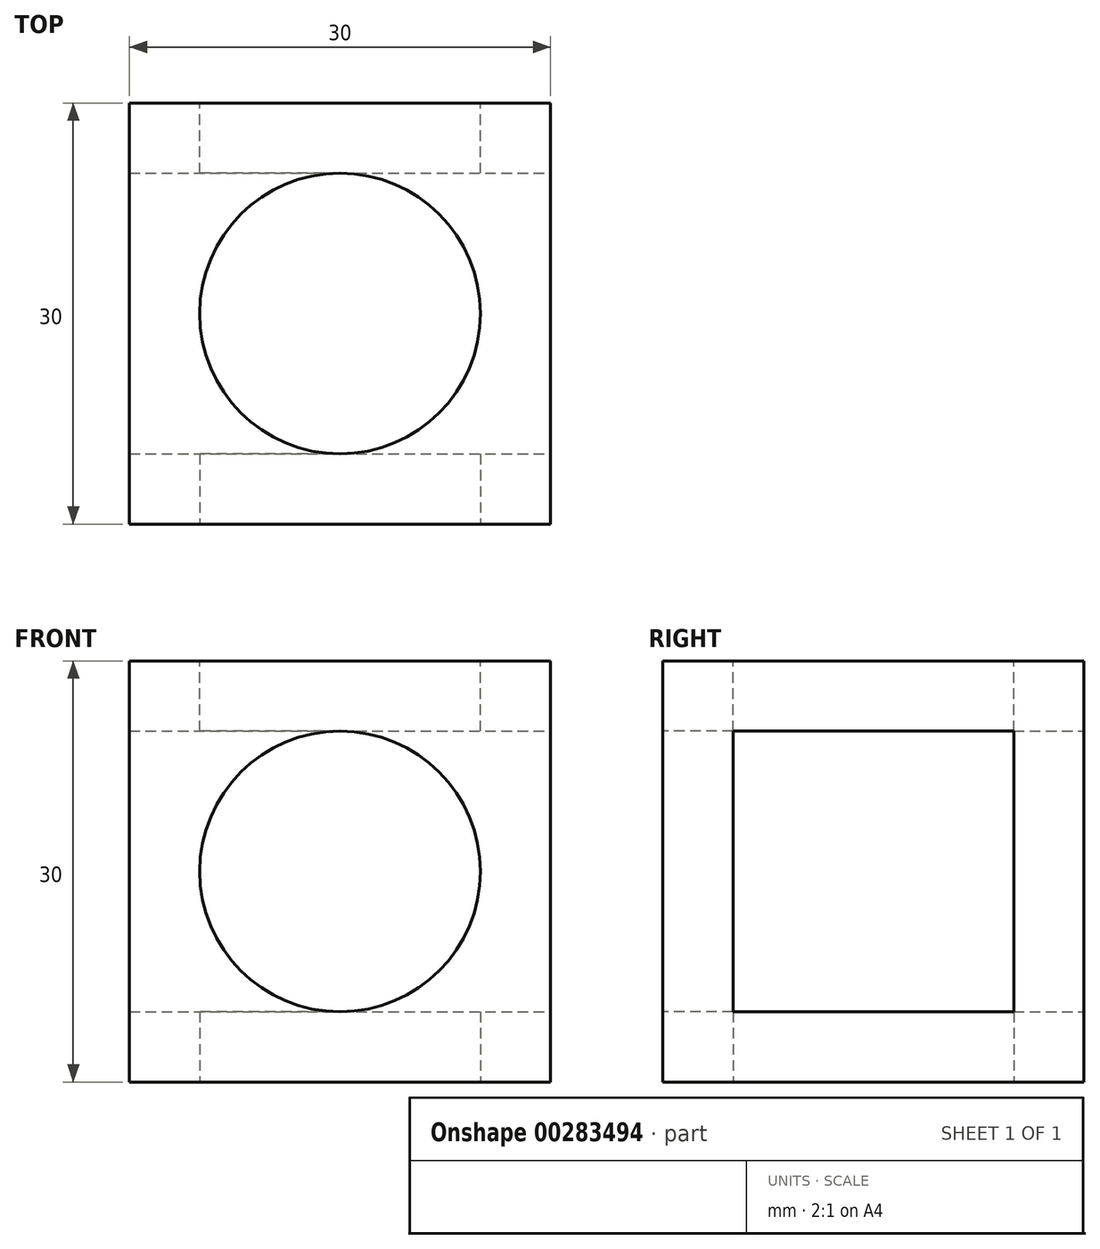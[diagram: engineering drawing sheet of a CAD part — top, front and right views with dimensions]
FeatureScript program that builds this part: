
annotation { "Feature Type Name" : "Feature", "Feature Type Description" : "" }
export const myFeature = defineFeature(function(context is Context, id is Id, definition is map)
    precondition{}
    {
        {
            var Q0;
            Q0=qCreatedBy(makeId("Right.planeOp"),FACE);
            var sketch = newSketch(context, id + "F0", { "sketchPlane" : qUnion([Q0])});
            skLineSegment(sketch, "E0.bottom", {"start": v(15, 15) * mm, "end": v(-15, 15) * mm});
            skLineSegment(sketch, "E0.top", {"start": v(15, -15) * mm, "end": v(-15, -15) * mm});
            skLineSegment(sketch, "E0.left", {"start": v(15, 15) * mm, "end": v(15, -15) * mm});
            skLineSegment(sketch, "E0.right", {"start": v(-15, 15) * mm, "end": v(-15, -15) * mm});
            skPoint(sketch, "E0.middle", {"position": v(0, 0) * mm});
            skSolve(sketch);
        }
        {
            var Q0;
            Q0=makeQuery(id+"F0.imprint","IMPRINT",FACE,{"disambiguationData":[TD([[makeQuery(id+"F0.imprint","IMPRINT",EDGE,{"derivedFrom":sQuery(id+"F0.wireOp",EDGE,"E0.bottom")}),1.0]])]});
            extrude(context, id + "F1", {"entities" : qUnion([Q0]), "depth" : 30 * mm});
        }
        {
            var Q0;
            Q0=makeQuery(id+"F1.opExtrude","CAP_FACE",FACE,{"disambiguationData":[OSD([sQuery(id+"F0.wireOp",EDGE,"E0.bottom"),sQuery(id+"F0.wireOp",EDGE,"E0.top"),sQuery(id+"F0.wireOp",EDGE,"E0.left"),sQuery(id+"F0.wireOp",EDGE,"E0.right")])],"isStart":false});
            var sketch = newSketch(context, id + "F2", { "sketchPlane" : qUnion([Q0])});
            skLineSegment(sketch, "E1.bottom", {"start": v(10, 10) * mm, "end": v(-10, 10) * mm});
            skLineSegment(sketch, "E1.top", {"start": v(10, -10) * mm, "end": v(-10, -10) * mm});
            skLineSegment(sketch, "E1.left", {"start": v(10, 10) * mm, "end": v(10, -10) * mm});
            skLineSegment(sketch, "E1.right", {"start": v(-10, 10) * mm, "end": v(-10, -10) * mm});
            skPoint(sketch, "E1.middle", {"position": v(0, 0) * mm});
            skSolve(sketch);
        }
        {
            var Q0;
            Q0=makeQuery(id+"F2.imprint","IMPRINT",FACE,{"disambiguationData":[TD([[makeQuery(id+"F2.imprint","IMPRINT",EDGE,{"derivedFrom":sQuery(id+"F2.wireOp",EDGE,"E1.bottom")}),1.0]])]});
            extrude(context, id + "F3", {"entities" : qUnion([Q0]), "operationType" : NewBodyOperationType.REMOVE, "endBound" : BoundingType.THROUGH_ALL, "oppositeDirection" : true, "depth" : 25 * mm});
        }
        {
            var Q0;
            Q0=makeQuery(id+"F1.opExtrude","SWEPT_FACE",FACE,{"disambiguationData":[OSD([sQuery(id+"F0.wireOp",EDGE,"E0.right")])]});
            var sketch = newSketch(context, id + "F4", { "sketchPlane" : qUnion([Q0])});
            skCircle(sketch, "E2", {"center": v(15, 0) * mm, "radius": 10 * mm});
            skLineSegment(sketch, "E3.JHt.JHt", {"start": v(30, 15) * mm, "end": v(30, -15) * mm, "construction": true});
            skLineSegment(sketch, "E3.JHF.JHF", {"start": v(30, 15) * mm, "end": v(0, 15) * mm, "construction": true});
            skArc(sketch, "E3.0.startCap", {"start": v(20, 15) * mm, "mid": v(30, 25) * mm, "end": v(40, 15) * mm});
            skArc(sketch, "E3.0.endCap", {"start": v(40, -15) * mm, "mid": v(30, -25) * mm, "end": v(20, -15) * mm});
            skLineSegment(sketch, "E3.0.left", {"start": v(40, 15) * mm, "end": v(40, -15) * mm});
            skLineSegment(sketch, "E3.0.right", {"start": v(20, 15) * mm, "end": v(20, -15) * mm});
            skArc(sketch, "E3.1.startCap", {"start": v(30, 25) * mm, "mid": v(40, 15) * mm, "end": v(30, 5) * mm});
            skArc(sketch, "E3.1.endCap", {"start": v(0, 5) * mm, "mid": v(-10, 15) * mm, "end": v(0, 25) * mm});
            skLineSegment(sketch, "E3.1.left", {"start": v(30, 5) * mm, "end": v(0, 5) * mm});
            skLineSegment(sketch, "E3.1.right", {"start": v(30, 25) * mm, "end": v(0, 25) * mm});
            skSolve(sketch);
        }
        {
            var Q0;
            Q0=makeQuery(id+"F4.imprint","IMPRINT",FACE,{"disambiguationData":[TD([[makeQuery(id+"F4.imprint","IMPRINT",EDGE,{"derivedFrom":sQuery(id+"F4.wireOp",EDGE,"E2")}),1.0]])]});
            extrude(context, id + "F5", {"entities" : qUnion([Q0]), "operationType" : NewBodyOperationType.REMOVE, "endBound" : BoundingType.UP_TO_NEXT, "oppositeDirection" : true, "depth" : 25 * mm});
        }
        {
            var Q0;
            Q0=makeQuery(id+"F1.opExtrude","SWEPT_FACE",FACE,{"disambiguationData":[OSD([sQuery(id+"F0.wireOp",EDGE,"E0.bottom")])]});
            var sketch = newSketch(context, id + "F6", { "sketchPlane" : qUnion([Q0])});
            skCircle(sketch, "E4", {"center": v(15, 0) * mm, "radius": 10 * mm});
            skSolve(sketch);
        }
        {
            var Q0;
            Q0=makeQuery(id+"F6.imprint","IMPRINT",FACE,{"disambiguationData":[TD([[makeQuery(id+"F6.imprint","IMPRINT",EDGE,{"derivedFrom":sQuery(id+"F6.wireOp",EDGE,"E4")}),1.0]])]});
            extrude(context, id + "F7", {"entities" : qUnion([Q0]), "operationType" : NewBodyOperationType.REMOVE, "endBound" : BoundingType.UP_TO_NEXT, "oppositeDirection" : true, "depth" : 25 * mm});
        }
        {
            var Q0;
            Q0=makeQuery(id+"F1.opExtrude","SWEPT_FACE",FACE,{"disambiguationData":[OSD([sQuery(id+"F0.wireOp",EDGE,"E0.left")])]});
            var sketch = newSketch(context, id + "F8", { "sketchPlane" : qUnion([Q0])});
            skCircle(sketch, "E5", {"center": v(-15, 0) * mm, "radius": 10 * mm});
            skSolve(sketch);
        }
        {
            var Q0;
            Q0=makeQuery(id+"F8.imprint","IMPRINT",FACE,{"disambiguationData":[TD([[makeQuery(id+"F8.imprint","IMPRINT",EDGE,{"derivedFrom":sQuery(id+"F8.wireOp",EDGE,"E5")}),1.0]])]});
            extrude(context, id + "F9", {"entities" : qUnion([Q0]), "operationType" : NewBodyOperationType.REMOVE, "endBound" : BoundingType.UP_TO_NEXT, "oppositeDirection" : true, "depth" : 25 * mm});
        }
        {
            var Q0;
            Q0=makeQuery(id+"F1.opExtrude","SWEPT_FACE",FACE,{"disambiguationData":[OSD([sQuery(id+"F0.wireOp",EDGE,"E0.top")])]});
            var sketch = newSketch(context, id + "F10", { "sketchPlane" : qUnion([Q0])});
            skCircle(sketch, "E6", {"center": v(15, 0) * mm, "radius": 10 * mm});
            skSolve(sketch);
        }
        {
            var Q0;
            Q0=makeQuery(id+"F10.imprint","IMPRINT",FACE,{"disambiguationData":[TD([[makeQuery(id+"F10.imprint","IMPRINT",EDGE,{"derivedFrom":sQuery(id+"F10.wireOp",EDGE,"E6")}),1.0]])]});
            extrude(context, id + "F11", {"entities" : qUnion([Q0]), "operationType" : NewBodyOperationType.REMOVE, "endBound" : BoundingType.UP_TO_NEXT, "oppositeDirection" : true, "depth" : 25 * mm});
        }
    });
